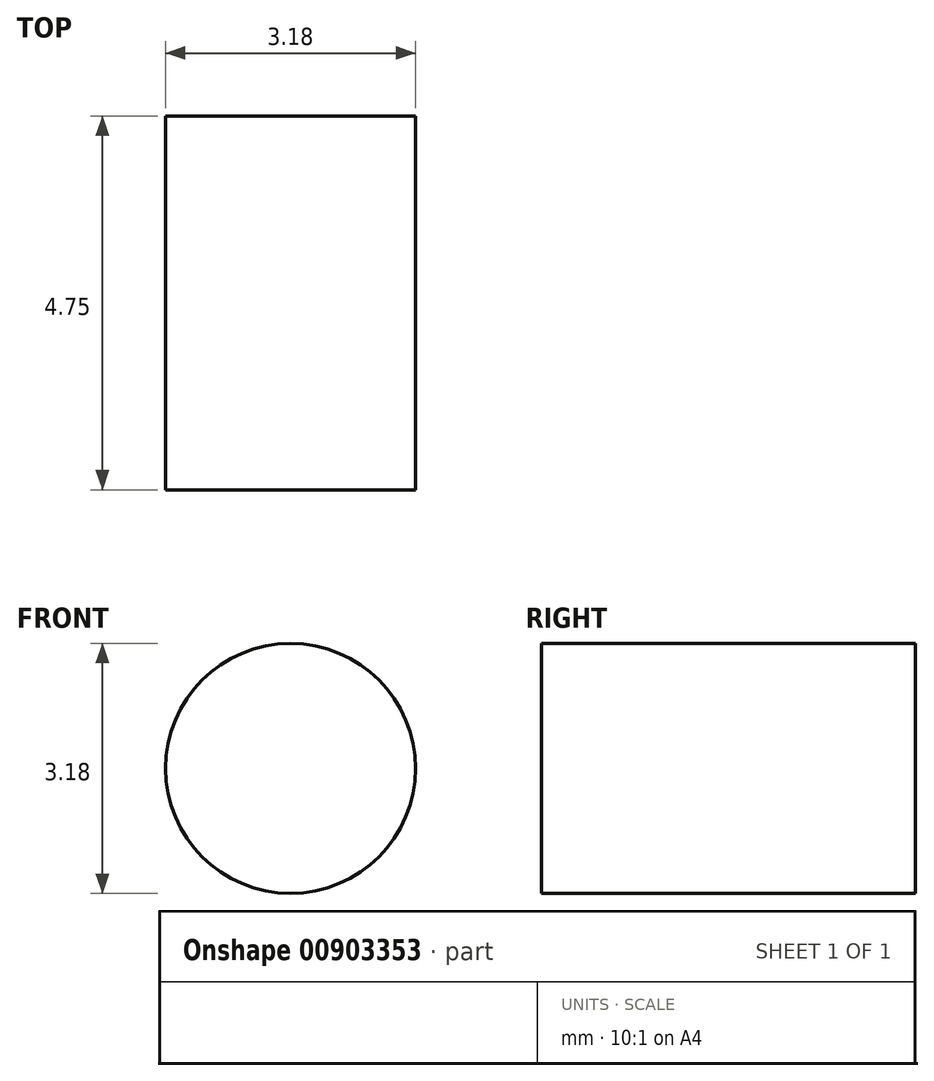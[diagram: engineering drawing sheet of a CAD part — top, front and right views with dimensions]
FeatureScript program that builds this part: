
annotation { "Feature Type Name" : "Feature", "Feature Type Description" : "" }
export const myFeature = defineFeature(function(context is Context, id is Id, definition is map)
    precondition{}
    {
        {
            var Q0;
            Q0=qCreatedBy(makeId("Front.planeOp"),FACE);
            var sketch = newSketch(context, id + "F0", { "sketchPlane" : qUnion([Q0])});
            skCircle(sketch, "E0", {"center": v(0, 0) * mm, "radius": 1.59 * mm});
            skSolve(sketch);
        }
        {
            var Q0;
            Q0=makeQuery(id+"F0.imprint","IMPRINT",FACE,{"disambiguationData":[TD([[makeQuery(id+"F0.imprint","IMPRINT",EDGE,{"derivedFrom":sQuery(id+"F0.wireOp",EDGE,"E0")}),1.0]])]});
            extrude(context, id + "F1", {"entities" : qUnion([Q0]), "oppositeDirection" : true, "depth" : 4.75 * mm, "offsetDistance" : 25.4 * mm});
        }
    });
